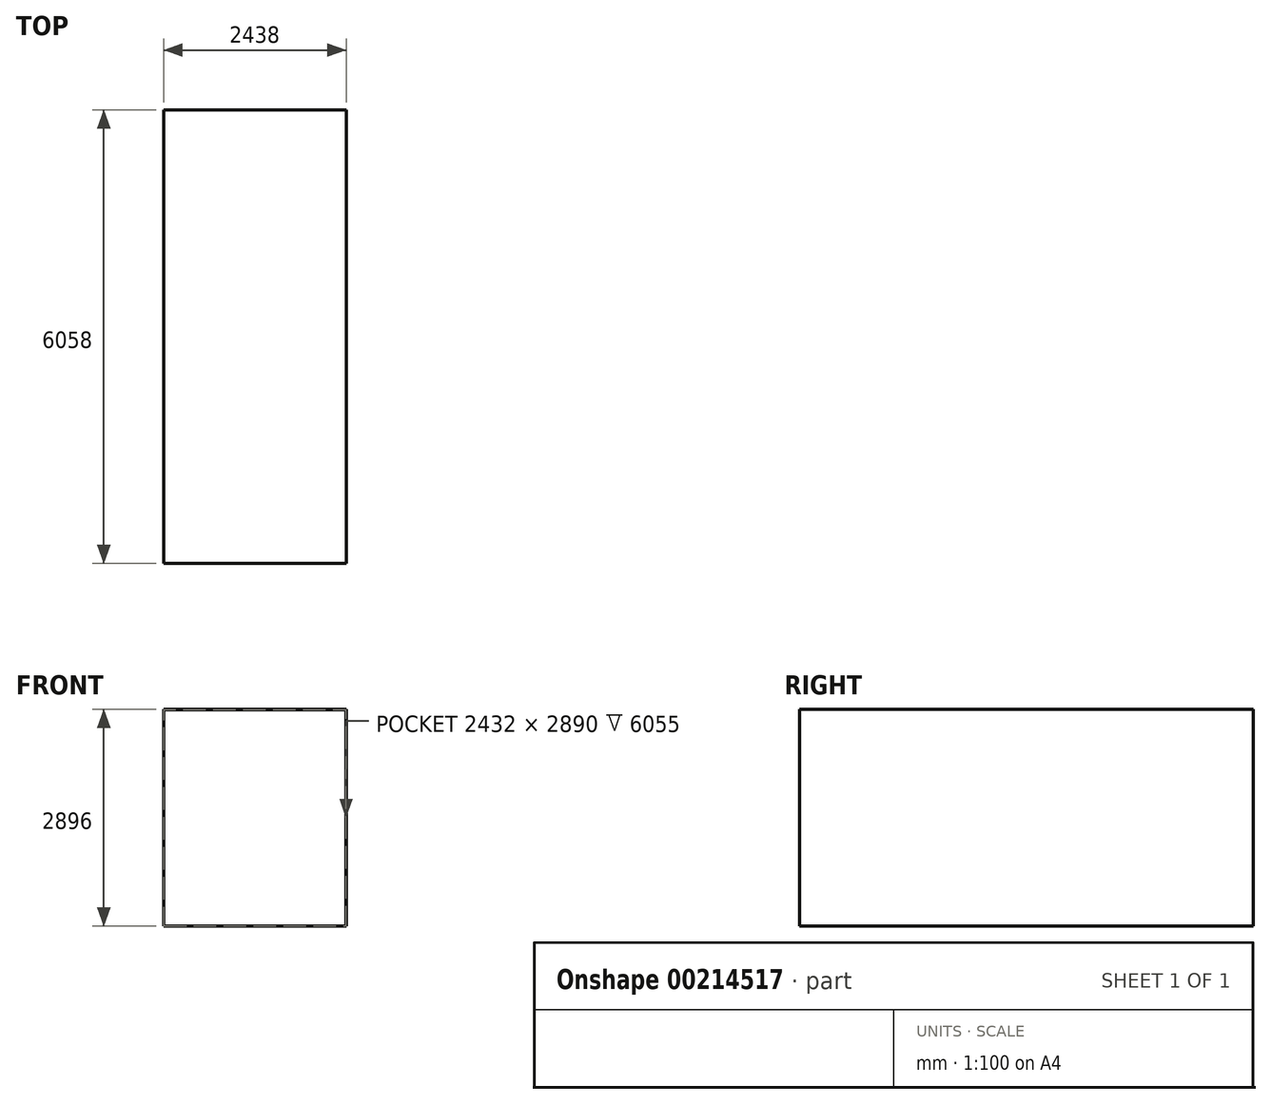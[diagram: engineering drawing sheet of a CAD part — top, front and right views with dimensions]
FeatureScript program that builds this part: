
annotation { "Feature Type Name" : "Feature", "Feature Type Description" : "" }
export const myFeature = defineFeature(function(context is Context, id is Id, definition is map)
    precondition{}
    {
        {
            var Q0;
            Q0=qCreatedBy(makeId("Front.planeOp"),FACE);
            var sketch = newSketch(context, id + "F0", { "sketchPlane" : qUnion([Q0])});
            skLineSegment(sketch, "E0.bottom", {"start": v(-1216, 1445) * mm, "end": v(1216, 1445) * mm});
            skLineSegment(sketch, "E0.top", {"start": v(-1216, -1445) * mm, "end": v(1216, -1445) * mm});
            skLineSegment(sketch, "E0.left", {"start": v(-1216, 1445) * mm, "end": v(-1216, -1445) * mm});
            skLineSegment(sketch, "E0.right", {"start": v(1216, 1445) * mm, "end": v(1216, -1445) * mm});
            skLineSegment(sketch, "E1.bottom", {"start": v(-1219, 1448) * mm, "end": v(1219, 1448) * mm});
            skLineSegment(sketch, "E1.top", {"start": v(-1219, -1448) * mm, "end": v(1219, -1448) * mm});
            skLineSegment(sketch, "E1.left", {"start": v(-1219, 1448) * mm, "end": v(-1219, -1448) * mm});
            skLineSegment(sketch, "E1.right", {"start": v(1219, 1448) * mm, "end": v(1219, -1448) * mm});
            skSolve(sketch);
        }
        {
            var Q0;
            Q0 = qSketchRegion(id + "F0", true);
            extrude(context, id + "F1", {"entities" : qUnion([Q0]), "depth" : 6058 * mm});
        }
        {
            var Q0;
            Q0=qCreatedBy(makeId("Front.planeOp"),FACE);
            var sketch = newSketch(context, id + "F2", { "sketchPlane" : qUnion([Q0])});
            skLineSegment(sketch, "E2.bottom", {"start": v(1219, 1448) * mm, "end": v(-1218.84, 1448) * mm});
            skLineSegment(sketch, "E2.top", {"start": v(1219, -1447.97) * mm, "end": v(-1218.84, -1447.97) * mm});
            skLineSegment(sketch, "E2.left", {"start": v(1219, 1448) * mm, "end": v(1219, -1447.97) * mm});
            skLineSegment(sketch, "E2.right", {"start": v(-1218.84, 1448) * mm, "end": v(-1218.84, -1447.97) * mm});
            skSolve(sketch);
        }
        {
            var Q0;
            Q0 = qSketchRegion(id + "F2", true);
            extrude(context, id + "F3", {"entities" : qUnion([Q0]), "operationType" : NewBodyOperationType.ADD, "depth" : 3 * mm});
        }
    });
